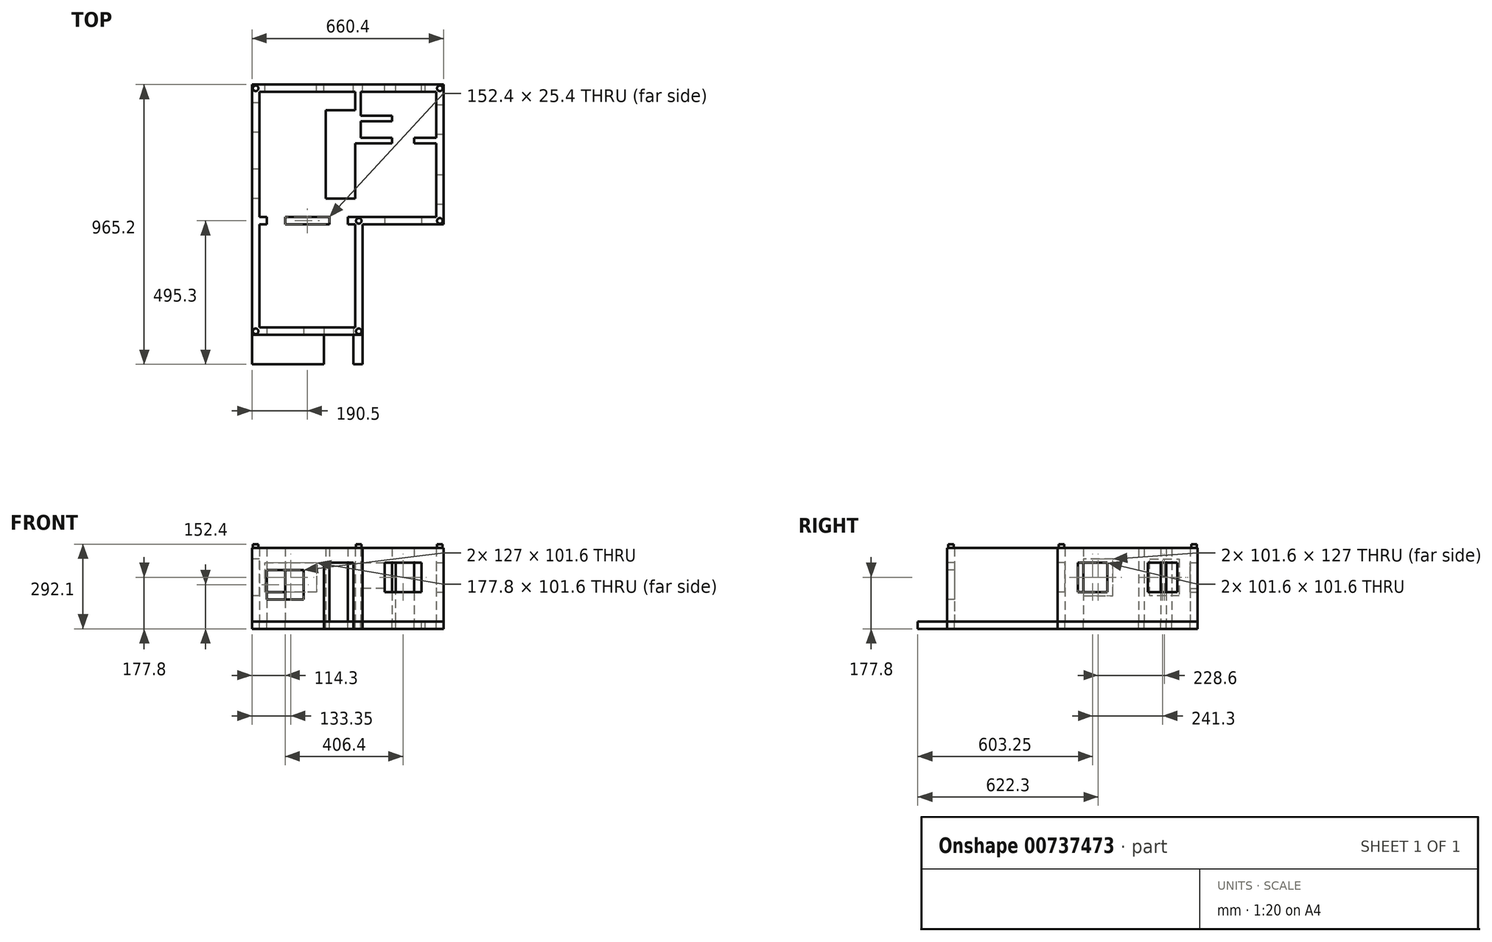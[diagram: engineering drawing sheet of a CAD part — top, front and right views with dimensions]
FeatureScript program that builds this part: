
annotation { "Feature Type Name" : "Feature", "Feature Type Description" : "" }
export const myFeature = defineFeature(function(context is Context, id is Id, definition is map)
    precondition{}
    {
        {
            var Q0;
            Q0=qCreatedBy(makeId("Top.planeOp"),FACE);
            var sketch = newSketch(context, id + "F0", { "sketchPlane" : qUnion([Q0])});
            skLineSegment(sketch, "E0", {"start": v(0, 0) * mm, "end": v(330.2, 0) * mm});
            skLineSegment(sketch, "E1", {"start": v(0, 0) * mm, "end": v(0, 381) * mm});
            skLineSegment(sketch, "E2", {"start": v(330.2, 0) * mm, "end": v(330.2, 381) * mm});
            skLineSegment(sketch, "E3", {"start": v(0, 381) * mm, "end": v(0, 812.8) * mm});
            skLineSegment(sketch, "E4", {"start": v(0, 812.8) * mm, "end": v(330.2, 812.8) * mm});
            skLineSegment(sketch, "E5", {"start": v(330.2, 381) * mm, "end": v(609.6, 381) * mm});
            skLineSegment(sketch, "E6", {"start": v(609.6, 381) * mm, "end": v(609.6, 812.8) * mm});
            skLineSegment(sketch, "E7", {"start": v(609.6, 635) * mm, "end": v(533.4, 635) * mm});
            skLineSegment(sketch, "E8", {"start": v(609.6, 812.8) * mm, "end": v(508, 812.8) * mm});
            skLineSegment(sketch, "E9", {"start": v(330.2, 812.8) * mm, "end": v(508, 812.8) * mm});
            skLineSegment(sketch, "E10", {"start": v(330.2, 672.42) * mm, "end": v(330.2, 812.8) * mm});
            skLineSegment(sketch, "E11", {"start": v(330.2, 635) * mm, "end": v(457.2, 635) * mm});
            skLineSegment(sketch, "E12", {"start": v(457.2, 711.2) * mm, "end": v(330.2, 711.2) * mm});
            skLineSegment(sketch, "E13", {"start": v(330.2, 0) * mm, "end": v(355.6, 0) * mm});
            skLineSegment(sketch, "E14", {"start": v(355.6, 0) * mm, "end": v(355.6, 355.6) * mm});
            skLineSegment(sketch, "E15", {"start": v(355.6, 355.6) * mm, "end": v(635, 355.6) * mm});
            skLineSegment(sketch, "E16", {"start": v(635, 355.6) * mm, "end": v(635, 838.2) * mm});
            skLineSegment(sketch, "E17", {"start": v(635, 838.2) * mm, "end": v(-25.4, 838.2) * mm});
            skLineSegment(sketch, "E18", {"start": v(-25.4, 838.2) * mm, "end": v(-25.4, -25.4) * mm});
            skLineSegment(sketch, "E19", {"start": v(-25.4, -25.4) * mm, "end": v(355.6, -25.4) * mm});
            skLineSegment(sketch, "E20", {"start": v(355.6, -25.4) * mm, "end": v(355.6, 0) * mm});
            skLineSegment(sketch, "E21", {"start": v(0, 381) * mm, "end": v(25.4, 381) * mm});
            skLineSegment(sketch, "E22", {"start": v(25.4, 381) * mm, "end": v(25.4, 355.6) * mm});
            skLineSegment(sketch, "E23", {"start": v(25.4, 355.6) * mm, "end": v(0, 355.6) * mm});
            skLineSegment(sketch, "E24", {"start": v(88.9, 381) * mm, "end": v(241.3, 381) * mm});
            skLineSegment(sketch, "E25", {"start": v(88.9, 381) * mm, "end": v(88.9, 355.6) * mm});
            skLineSegment(sketch, "E26", {"start": v(88.9, 355.6) * mm, "end": v(241.3, 355.6) * mm});
            skLineSegment(sketch, "E27", {"start": v(241.3, 355.6) * mm, "end": v(241.3, 381) * mm});
            skLineSegment(sketch, "E28", {"start": v(304.8, 355.6) * mm, "end": v(304.8, 381) * mm});
            skLineSegment(sketch, "E29", {"start": v(304.8, 381) * mm, "end": v(330.2, 381) * mm});
            skLineSegment(sketch, "E30", {"start": v(304.8, 355.6) * mm, "end": v(330.2, 355.6) * mm});
            skLineSegment(sketch, "E31", {"start": v(330.2, 672.42) * mm, "end": v(330.2, 635) * mm});
            skLineSegment(sketch, "E32", {"start": v(228.6, 749.3) * mm, "end": v(330.2, 749.3) * mm});
            skLineSegment(sketch, "E33", {"start": v(330.2, 635) * mm, "end": v(330.2, 444.5) * mm});
            skLineSegment(sketch, "E34", {"start": v(330.2, 444.5) * mm, "end": v(228.6, 444.5) * mm});
            skLineSegment(sketch, "E35", {"start": v(228.6, 444.5) * mm, "end": v(228.6, 749.3) * mm});
            skLineSegment(sketch, "E36", {"start": v(457.2, 711.2) * mm, "end": v(457.2, 730.25) * mm});
            skLineSegment(sketch, "E37", {"start": v(457.2, 635) * mm, "end": v(457.2, 654.05) * mm});
            skLineSegment(sketch, "E38", {"start": v(457.2, 654.05) * mm, "end": v(349.25, 654.05) * mm});
            skLineSegment(sketch, "E39", {"start": v(349.25, 654.05) * mm, "end": v(349.25, 711.2) * mm});
            skLineSegment(sketch, "E40", {"start": v(533.4, 635) * mm, "end": v(533.4, 654.05) * mm});
            skLineSegment(sketch, "E41", {"start": v(533.4, 654.05) * mm, "end": v(609.6, 654.05) * mm});
            skLineSegment(sketch, "E42", {"start": v(457.2, 730.25) * mm, "end": v(349.25, 730.25) * mm});
            skLineSegment(sketch, "E43", {"start": v(349.25, 730.25) * mm, "end": v(349.25, 812.8) * mm});
            skSolve(sketch);
        }
        {
            var Q0;
            {var subQ8=sQuery(id+"F0.wireOp",EDGE,"E0");Q0=makeQuery(id+"F0.imprint","IMPRINT",FACE,{"disambiguationData":[TD([[makeQuery(id+"F0.imprint","IMPRINT",EDGE,{"derivedFrom":subQ8}),-1.0]])]});}
            var Q1;
            Q1=makeQuery(id+"F0.imprint","IMPRINT",FACE,{"disambiguationData":[TD([[makeQuery(id+"F0.imprint","IMPRINT",EDGE,{"derivedFrom":sQuery(id+"F0.wireOp",EDGE,"E24")}),-1.0]])]});
            var Q2;
            {var subQ0=sQuery(id+"F0.wireOp",EDGE,"E21");Q2=makeQuery(id+"F0.imprint","IMPRINT",FACE,{"disambiguationData":[TD([[makeQuery(id+"F0.imprint","IMPRINT",EDGE,{"derivedFrom":subQ0}),-1.0]])]});}
            var Q3;
            Q3=makeQuery(id+"F0.imprint","IMPRINT",FACE,{"disambiguationData":[TD([[makeQuery(id+"F0.imprint","IMPRINT",EDGE,{"derivedFrom":sQuery(id+"F0.wireOp",EDGE,"E28")}),-1.0]])]});
            var Q4;
            {var subQ3=sQuery(id+"F0.wireOp",EDGE,"E31");Q4=makeQuery(id+"F0.imprint","IMPRINT",FACE,{"disambiguationData":[TD([[makeQuery(id+"F0.imprint","IMPRINT",EDGE,{"derivedFrom":subQ3}),-1.0]])]});}
            var Q5;
            {var subQ0=sQuery(id+"F0.wireOp",EDGE,"E36");Q5=makeQuery(id+"F0.imprint","IMPRINT",FACE,{"disambiguationData":[TD([[makeQuery(id+"F0.imprint","IMPRINT",EDGE,{"derivedFrom":subQ0}),1.0]])]});}
            var Q6;
            Q6=makeQuery(id+"F0.imprint","IMPRINT",FACE,{"disambiguationData":[TD([[makeQuery(id+"F0.imprint","IMPRINT",EDGE,{"derivedFrom":sQuery(id+"F0.wireOp",EDGE,"E11")}),1.0]])]});
            var Q7;
            {var subQ0=sQuery(id+"F0.wireOp",EDGE,"E7");Q7=makeQuery(id+"F0.imprint","IMPRINT",FACE,{"disambiguationData":[TD([[makeQuery(id+"F0.imprint","IMPRINT",EDGE,{"derivedFrom":subQ0}),-1.0]])]});}
            extrude(context, id + "F1", {"entities" : qUnion([Q0, Q1, Q2, Q3, Q4, Q5, Q6, Q7]), "depth" : 254 * mm, "offsetDistance" : 25.4 * mm});
        }
        {
            var Q0;
            {var subQ10=sQuery(id+"F0.wireOp",EDGE,"E0");Q0=makeQuery(id+"F0.imprint","IMPRINT",FACE,{"disambiguationData":[TD([[makeQuery(id+"F0.imprint","IMPRINT",EDGE,{"derivedFrom":subQ10}),1.0]])]});}
            extrude(context, id + "F2", {"entities" : qUnion([Q0]), "oppositeDirection" : true, "depth" : 25.4 * mm, "offsetDistance" : 25.4 * mm});
        }
        {
            var Q0;
            Q0=makeQuery(id+"F1.opExtrude","CAP_FACE",FACE,{"disambiguationData":[OSD([sQuery(id+"F0.wireOp",EDGE,"E0"),sQuery(id+"F0.wireOp",EDGE,"E1"),sQuery(id+"F0.wireOp",EDGE,"E2"),sQuery(id+"F0.wireOp",EDGE,"E3"),sQuery(id+"F0.wireOp",EDGE,"E4"),sQuery(id+"F0.wireOp",EDGE,"E5"),sQuery(id+"F0.wireOp",EDGE,"E6"),sQuery(id+"F0.wireOp",EDGE,"E7"),sQuery(id+"F0.wireOp",EDGE,"E8"),sQuery(id+"F0.wireOp",EDGE,"E9"),sQuery(id+"F0.wireOp",EDGE,"E10"),sQuery(id+"F0.wireOp",EDGE,"E11"),sQuery(id+"F0.wireOp",EDGE,"E12"),sQuery(id+"F0.wireOp",EDGE,"E14"),sQuery(id+"F0.wireOp",EDGE,"E15"),sQuery(id+"F0.wireOp",EDGE,"E16"),sQuery(id+"F0.wireOp",EDGE,"E17"),sQuery(id+"F0.wireOp",EDGE,"E18"),sQuery(id+"F0.wireOp",EDGE,"E19"),sQuery(id+"F0.wireOp",EDGE,"E20"),sQuery(id+"F0.wireOp",EDGE,"E21"),sQuery(id+"F0.wireOp",EDGE,"E22"),sQuery(id+"F0.wireOp",EDGE,"E23"),sQuery(id+"F0.wireOp",EDGE,"E28"),sQuery(id+"F0.wireOp",EDGE,"E29"),sQuery(id+"F0.wireOp",EDGE,"E30"),sQuery(id+"F0.wireOp",EDGE,"E32"),sQuery(id+"F0.wireOp",EDGE,"E33"),sQuery(id+"F0.wireOp",EDGE,"E34"),sQuery(id+"F0.wireOp",EDGE,"E35"),sQuery(id+"F0.wireOp",EDGE,"E36"),sQuery(id+"F0.wireOp",EDGE,"E37"),sQuery(id+"F0.wireOp",EDGE,"E38"),sQuery(id+"F0.wireOp",EDGE,"E39"),sQuery(id+"F0.wireOp",EDGE,"E40"),sQuery(id+"F0.wireOp",EDGE,"E41"),sQuery(id+"F0.wireOp",EDGE,"E42"),sQuery(id+"F0.wireOp",EDGE,"E43")])],"isStart":false});
            var sketch = newSketch(context, id + "F3", { "sketchPlane" : qUnion([Q0])});
            skLineSegment(sketch, "E44", {"start": v(0, 0) * mm, "end": v(-25.4, 0) * mm});
            skLineSegment(sketch, "E45", {"start": v(0, 0) * mm, "end": v(0, -25.4) * mm});
            skLineSegment(sketch, "E46", {"start": v(330.2, 0) * mm, "end": v(330.2, -25.4) * mm});
            skLineSegment(sketch, "E47", {"start": v(330.2, 0) * mm, "end": v(355.6, 0) * mm});
            skLineSegment(sketch, "E48", {"start": v(330.2, 355.6) * mm, "end": v(330.2, 381) * mm});
            skLineSegment(sketch, "E49", {"start": v(330.2, 355.6) * mm, "end": v(355.6, 355.6) * mm});
            skLineSegment(sketch, "E50", {"start": v(355.6, 355.6) * mm, "end": v(355.6, 381) * mm});
            skLineSegment(sketch, "E51", {"start": v(609.6, 381) * mm, "end": v(609.6, 355.6) * mm});
            skLineSegment(sketch, "E52", {"start": v(609.6, 381) * mm, "end": v(635, 381) * mm});
            skLineSegment(sketch, "E53", {"start": v(609.6, 812.8) * mm, "end": v(609.6, 838.2) * mm});
            skLineSegment(sketch, "E54", {"start": v(609.6, 812.8) * mm, "end": v(635, 812.8) * mm});
            skLineSegment(sketch, "E55", {"start": v(-25.4, 812.8) * mm, "end": v(0, 812.8) * mm});
            skLineSegment(sketch, "E56", {"start": v(0, 812.8) * mm, "end": v(0, 838.2) * mm});
            skCircle(sketch, "E57", {"center": v(-12.7, -12.7) * mm, "radius": 9.53 * mm});
            skPoint(sketch, "E57.centerSnap0", {"position": v(-12.7, 0) * mm});
            skPoint(sketch, "E57.centerSnap1", {"position": v(0, -12.7) * mm});
            skPoint(sketch, "E58.centerSnap0", {"position": v(330.2, -12.7) * mm});
            skPoint(sketch, "E58.centerSnap1", {"position": v(342.9, 0) * mm});
            skCircle(sketch, "E59", {"center": v(342.9, -12.7) * mm, "radius": 9.53 * mm});
            skCircle(sketch, "E60", {"center": v(342.9, 368.3) * mm, "radius": 9.53 * mm});
            skPoint(sketch, "E60.centerSnap0", {"position": v(342.9, 355.6) * mm});
            skPoint(sketch, "E60.centerSnap1", {"position": v(330.2, 368.3) * mm});
            skCircle(sketch, "E61", {"center": v(622.3, 368.3) * mm, "radius": 9.53 * mm});
            skPoint(sketch, "E61.centerSnap0", {"position": v(609.6, 368.3) * mm});
            skPoint(sketch, "E61.centerSnap1", {"position": v(622.3, 381) * mm});
            skCircle(sketch, "E62", {"center": v(622.3, 825.5) * mm, "radius": 9.53 * mm});
            skPoint(sketch, "E62.centerSnap0", {"position": v(609.6, 825.5) * mm});
            skPoint(sketch, "E62.centerSnap1", {"position": v(622.3, 812.8) * mm});
            skCircle(sketch, "E63", {"center": v(-12.7, 825.5) * mm, "radius": 9.53 * mm});
            skPoint(sketch, "E63.centerSnap0", {"position": v(-12.7, 812.8) * mm});
            skPoint(sketch, "E63.centerSnap1", {"position": v(0, 825.5) * mm});
            skSolve(sketch);
        }
        {
            var Q0;
            Q0=qSketchRegion(id+"F3",true);
            extrude(context, id + "F4", {"entities" : qUnion([Q0]), "operationType" : NewBodyOperationType.ADD, "depth" : 12.7 * mm, "offsetDistance" : 25.4 * mm});
        }
        {
            var Q0;
            Q0=makeQuery(id+"F1.opExtrude","SWEPT_FACE",FACE,{"disambiguationData":[OSD([sQuery(id+"F0.wireOp",EDGE,"E19")])]});
            var sketch = newSketch(context, id + "F5", { "sketchPlane" : qUnion([Q0])});
            skLineSegment(sketch, "E64", {"start": v(-25.4, 0) * mm, "end": v(-25.4, 76.2) * mm});
            skLineSegment(sketch, "E65", {"start": v(25.4, 76.2) * mm, "end": v(152.4, 76.2) * mm});
            skLineSegment(sketch, "E66", {"start": v(152.4, 76.2) * mm, "end": v(152.4, 177.8) * mm});
            skLineSegment(sketch, "E67", {"start": v(152.4, 177.8) * mm, "end": v(25.4, 177.8) * mm});
            skLineSegment(sketch, "E68", {"start": v(25.4, 177.8) * mm, "end": v(25.4, 76.2) * mm});
            skSolve(sketch);
        }
        {
            var Q0;
            Q0=makeQuery(id+"F5.imprint","IMPRINT",FACE,{"disambiguationData":[TD([[makeQuery(id+"F5.imprint","IMPRINT",EDGE,{"derivedFrom":sQuery(id+"F5.wireOp",EDGE,"E65")}),1.0]])]});
            extrude(context, id + "F6", {"entities" : qUnion([Q0]), "operationType" : NewBodyOperationType.REMOVE, "oppositeDirection" : true, "depth" : 25.4 * mm, "offsetDistance" : 25.4 * mm});
        }
        {
            var Q0;
            Q0=makeQuery(id+"F1.opExtrude","SWEPT_FACE",FACE,{"disambiguationData":[OSD([sQuery(id+"F0.wireOp",EDGE,"E19")])]});
            var sketch = newSketch(context, id + "F7", { "sketchPlane" : qUnion([Q0])});
            skLineSegment(sketch, "E69", {"start": v(323.85, 0) * mm, "end": v(323.85, 203.2) * mm});
            skLineSegment(sketch, "E70", {"start": v(323.85, 203.2) * mm, "end": v(222.25, 203.2) * mm});
            skLineSegment(sketch, "E71", {"start": v(222.25, 203.2) * mm, "end": v(222.25, 0) * mm});
            skLineSegment(sketch, "E72", {"start": v(222.25, 0) * mm, "end": v(323.85, 0) * mm});
            skSolve(sketch);
        }
        {
            var Q0;
            Q0=qSketchRegion(id+"F7",true);
            extrude(context, id + "F8", {"entities" : qUnion([Q0]), "operationType" : NewBodyOperationType.REMOVE, "oppositeDirection" : true, "depth" : 25.4 * mm, "offsetDistance" : 25.4 * mm});
        }
        {
            var Q0;
            Q0=makeQuery(id+"F1.opExtrude","SWEPT_FACE",FACE,{"disambiguationData":[OSD([sQuery(id+"F0.wireOp",EDGE,"E15")])]});
            var sketch = newSketch(context, id + "F9", { "sketchPlane" : qUnion([Q0])});
            skLineSegment(sketch, "E73", {"start": v(395.93, 254) * mm, "end": v(395.93, 0) * mm});
            skLineSegment(sketch, "E74", {"start": v(355.6, 231.93) * mm, "end": v(635, 231.93) * mm});
            skPoint(sketch, "E75.startSnap0", {"position": v(395.93, 127) * mm});
            skPoint(sketch, "E75.startSnap1", {"position": v(495.3, 231.93) * mm});
            skLineSegment(sketch, "E76", {"start": v(495.3, 101.6) * mm, "end": v(431.8, 101.6) * mm});
            skLineSegment(sketch, "E77", {"start": v(431.8, 101.6) * mm, "end": v(431.8, 203.2) * mm});
            skLineSegment(sketch, "E78", {"start": v(431.8, 203.2) * mm, "end": v(558.8, 203.2) * mm});
            skLineSegment(sketch, "E79", {"start": v(558.8, 203.2) * mm, "end": v(558.8, 101.6) * mm});
            skLineSegment(sketch, "E80", {"start": v(558.8, 101.6) * mm, "end": v(495.3, 101.6) * mm});
            skSolve(sketch);
        }
        {
            var Q0;
            Q0=qSketchRegion(id+"F9",true);
            extrude(context, id + "F10", {"entities" : qUnion([Q0]), "operationType" : NewBodyOperationType.REMOVE, "oppositeDirection" : true, "depth" : 25.4 * mm, "offsetDistance" : 25.4 * mm});
        }
        {
            var Q0;
            Q0=makeQuery(id+"F1.opExtrude","SWEPT_FACE",FACE,{"disambiguationData":[OSD([sQuery(id+"F0.wireOp",EDGE,"E16")])]});
            var sketch = newSketch(context, id + "F11", { "sketchPlane" : qUnion([Q0])});
            skLineSegment(sketch, "E81", {"start": v(355.6, 254) * mm, "end": v(838.2, 254) * mm});
            skLineSegment(sketch, "E82", {"start": v(596.9, 254) * mm, "end": v(596.9, 0) * mm});
            skLineSegment(sketch, "E83", {"start": v(355.6, 254) * mm, "end": v(596.9, 254) * mm});
            skLineSegment(sketch, "E84", {"start": v(476.25, 203.2) * mm, "end": v(425.45, 203.2) * mm});
            skLineSegment(sketch, "E85", {"start": v(425.45, 203.2) * mm, "end": v(425.45, 101.6) * mm});
            skLineSegment(sketch, "E86", {"start": v(425.45, 101.6) * mm, "end": v(527.05, 101.6) * mm});
            skLineSegment(sketch, "E87", {"start": v(527.05, 101.6) * mm, "end": v(527.05, 203.2) * mm});
            skLineSegment(sketch, "E88", {"start": v(527.05, 203.2) * mm, "end": v(476.25, 203.2) * mm});
            skLineSegment(sketch, "E89", {"start": v(596.9, 254) * mm, "end": v(838.2, 254) * mm});
            skLineSegment(sketch, "E90", {"start": v(717.55, 203.2) * mm, "end": v(666.75, 203.2) * mm});
            skLineSegment(sketch, "E91", {"start": v(666.75, 203.2) * mm, "end": v(666.75, 101.6) * mm});
            skLineSegment(sketch, "E92", {"start": v(666.75, 101.6) * mm, "end": v(768.35, 101.6) * mm});
            skLineSegment(sketch, "E93", {"start": v(768.35, 101.6) * mm, "end": v(768.35, 203.2) * mm});
            skLineSegment(sketch, "E94", {"start": v(768.35, 203.2) * mm, "end": v(717.55, 203.2) * mm});
            skSolve(sketch);
        }
        {
            var Q0;
            Q0=qSketchRegion(id+"F11",true);
            extrude(context, id + "F12", {"entities" : qUnion([Q0]), "operationType" : NewBodyOperationType.REMOVE, "oppositeDirection" : true, "depth" : 25.4 * mm, "offsetDistance" : 25.4 * mm});
        }
        {
            var Q0;
            Q0=qSketchRegion(id+"F11",true);
            extrude(context, id + "F13", {"entities" : qUnion([Q0]), "operationType" : NewBodyOperationType.REMOVE, "oppositeDirection" : true, "depth" : 25.4 * mm, "offsetDistance" : 25.4 * mm});
        }
        {
            var Q0;
            Q0=makeQuery(id+"F1.opExtrude","SWEPT_FACE",FACE,{"disambiguationData":[OSD([sQuery(id+"F0.wireOp",EDGE,"E18")])]});
            var sketch = newSketch(context, id + "F14", { "sketchPlane" : qUnion([Q0])});
            skLineSegment(sketch, "E95", {"start": v(-838.2, 254) * mm, "end": v(-381, 254) * mm});
            skLineSegment(sketch, "E96", {"start": v(-381, 254) * mm, "end": v(-381, 0) * mm});
            skLineSegment(sketch, "E97", {"start": v(-609.6, 254) * mm, "end": v(-609.6, 0) * mm});
            skLineSegment(sketch, "E98", {"start": v(-838.2, 254) * mm, "end": v(-609.6, 254) * mm});
            skLineSegment(sketch, "E99", {"start": v(-723.9, 215.9) * mm, "end": v(-774.7, 215.9) * mm});
            skLineSegment(sketch, "E100", {"start": v(-774.7, 215.9) * mm, "end": v(-774.7, 88.9) * mm});
            skLineSegment(sketch, "E101", {"start": v(-774.7, 88.9) * mm, "end": v(-673.1, 88.9) * mm});
            skLineSegment(sketch, "E102", {"start": v(-673.1, 88.9) * mm, "end": v(-673.1, 215.9) * mm});
            skLineSegment(sketch, "E103", {"start": v(-673.1, 215.9) * mm, "end": v(-723.9, 215.9) * mm});
            skLineSegment(sketch, "E104.MirrorCS", {"start": v(-546.1, 88.9) * mm, "end": v(-546.1, 215.9) * mm});
            skLineSegment(sketch, "E105.MirrorCS", {"start": v(-546.1, 215.9) * mm, "end": v(-495.3, 215.9) * mm});
            skLineSegment(sketch, "E106.MirrorCS", {"start": v(-495.3, 215.9) * mm, "end": v(-444.5, 215.9) * mm});
            skLineSegment(sketch, "E107.MirrorCS", {"start": v(-444.5, 215.9) * mm, "end": v(-444.5, 88.9) * mm});
            skLineSegment(sketch, "E108.MirrorCS", {"start": v(-444.5, 88.9) * mm, "end": v(-546.1, 88.9) * mm});
            skSolve(sketch);
        }
        {
            var Q0;
            Q0=qSketchRegion(id+"F14",true);
            extrude(context, id + "F15", {"entities" : qUnion([Q0]), "operationType" : NewBodyOperationType.REMOVE, "oppositeDirection" : true, "depth" : 25.4 * mm, "offsetDistance" : 25.4 * mm});
        }
        {
            var Q0;
            Q0=qSketchRegion(id+"F14",true);
            extrude(context, id + "F16", {"entities" : qUnion([Q0]), "operationType" : NewBodyOperationType.REMOVE, "oppositeDirection" : true, "depth" : 25.4 * mm, "offsetDistance" : 25.4 * mm});
        }
        {
            var Q0;
            Q0=makeQuery(id+"F1.opExtrude","SWEPT_FACE",FACE,{"disambiguationData":[OSD([sQuery(id+"F0.wireOp",EDGE,"E17")])]});
            var sketch = newSketch(context, id + "F17", { "sketchPlane" : qUnion([Q0])});
            skLineSegment(sketch, "E109", {"start": v(25.4, 254) * mm, "end": v(-330.2, 254) * mm});
            skLineSegment(sketch, "E110", {"start": v(-330.2, 254) * mm, "end": v(-330.2, 0) * mm});
            skPoint(sketch, "E111.endSnap0", {"position": v(-152.4, 254) * mm});
            skLineSegment(sketch, "E112", {"start": v(-222.25, 0) * mm, "end": v(-222.25, 203.2) * mm});
            skLineSegment(sketch, "E113", {"start": v(-222.25, 203.2) * mm, "end": v(-323.85, 203.2) * mm});
            skLineSegment(sketch, "E114", {"start": v(-323.85, 203.2) * mm, "end": v(-323.85, 0) * mm});
            skLineSegment(sketch, "E115", {"start": v(-323.85, 0) * mm, "end": v(-222.25, 0) * mm});
            skLineSegment(sketch, "E116", {"start": v(-196.85, 203.2) * mm, "end": v(-196.85, 101.6) * mm});
            skLineSegment(sketch, "E117", {"start": v(-196.85, 101.6) * mm, "end": v(-19.05, 101.6) * mm});
            skLineSegment(sketch, "E118", {"start": v(-19.05, 101.6) * mm, "end": v(-19.05, 203.2) * mm});
            skLineSegment(sketch, "E119", {"start": v(-19.05, 203.2) * mm, "end": v(-196.85, 203.2) * mm});
            skSolve(sketch);
        }
        {
            var Q0;
            Q0=qSketchRegion(id+"F17",true);
            extrude(context, id + "F18", {"entities" : qUnion([Q0]), "operationType" : NewBodyOperationType.REMOVE, "oppositeDirection" : true, "depth" : 25.4 * mm, "offsetDistance" : 25.4 * mm});
        }
        {
            var Q0;
            Q0=qSketchRegion(id+"F17",true);
            extrude(context, id + "F19", {"entities" : qUnion([Q0]), "operationType" : NewBodyOperationType.REMOVE, "oppositeDirection" : true, "depth" : 25.4 * mm, "offsetDistance" : 25.4 * mm});
        }
        {
            var Q0;
            Q0=makeQuery(id+"F1.opExtrude","SWEPT_FACE",FACE,{"disambiguationData":[OSD([sQuery(id+"F0.wireOp",EDGE,"E17")])]});
            var sketch = newSketch(context, id + "F20", { "sketchPlane" : qUnion([Q0])});
            skLineSegment(sketch, "E120", {"start": v(-635, 254) * mm, "end": v(-355.6, 254) * mm});
            skLineSegment(sketch, "E121", {"start": v(-355.6, 139.7) * mm, "end": v(-355.6, 203.2) * mm});
            skLineSegment(sketch, "E122", {"start": v(-355.6, 203.2) * mm, "end": v(-431.8, 203.2) * mm});
            skLineSegment(sketch, "E123", {"start": v(-431.8, 203.2) * mm, "end": v(-431.8, 114.3) * mm});
            skLineSegment(sketch, "E124", {"start": v(-431.8, 114.3) * mm, "end": v(-355.6, 114.3) * mm});
            skLineSegment(sketch, "E125", {"start": v(-355.6, 114.3) * mm, "end": v(-355.6, 139.7) * mm});
            skLineSegment(sketch, "E126", {"start": v(-431.8, 114.3) * mm, "end": v(-469.9, 114.3) * mm});
            skLineSegment(sketch, "E127", {"start": v(-469.9, 114.3) * mm, "end": v(-469.9, 203.2) * mm});
            skLineSegment(sketch, "E128", {"start": v(-469.9, 203.2) * mm, "end": v(-558.8, 203.2) * mm});
            skLineSegment(sketch, "E129", {"start": v(-558.8, 203.2) * mm, "end": v(-558.8, 0) * mm});
            skLineSegment(sketch, "E130", {"start": v(-558.8, 0) * mm, "end": v(-469.9, 0) * mm});
            skLineSegment(sketch, "E131", {"start": v(-469.9, 0) * mm, "end": v(-469.9, 114.3) * mm});
            skSolve(sketch);
        }
        {
            var Q0;
            Q0=makeQuery(id+"F20.imprint","IMPRINT",FACE,{"disambiguationData":[TD([[makeQuery(id+"F20.imprint","IMPRINT",EDGE,{"derivedFrom":sQuery(id+"F20.wireOp",EDGE,"E121")}),1.0]])]});
            extrude(context, id + "F21", {"entities" : qUnion([Q0]), "operationType" : NewBodyOperationType.REMOVE, "oppositeDirection" : true, "depth" : 25.4 * mm, "offsetDistance" : 25.4 * mm});
        }
        {
            var Q0;
            Q0=qSketchRegion(id+"F20",true);
            extrude(context, id + "F22", {"entities" : qUnion([Q0]), "operationType" : NewBodyOperationType.REMOVE, "oppositeDirection" : true, "depth" : 25.4 * mm, "offsetDistance" : 25.4 * mm});
        }
        {
            var Q0;
            {var subQ0=sQuery(id+"F0.wireOp",EDGE,"E32");var subQ2=sQuery(id+"F0.wireOp",EDGE,"E17");var subQ4=sQuery(id+"F0.wireOp",EDGE,"E12");var subQ6=sQuery(id+"F0.wireOp",EDGE,"E37");var subQ8=sQuery(id+"F0.wireOp",EDGE,"E4");var subQ9=makeQuery(id+"F1.opExtrude","SWEPT_FACE",FACE,{"disambiguationData":[OSD([subQ8])]});var subQ10=sQuery(id+"F0.wireOp",EDGE,"E33");var subQ12=sQuery(id+"F0.wireOp",EDGE,"E9");var subQ13=sQuery(id+"F0.wireOp",EDGE,"E8");var subQ15=sQuery(id+"F0.wireOp",EDGE,"E34");var subQ17=sQuery(id+"F0.wireOp",EDGE,"E10");var subQ19=sQuery(id+"F0.wireOp",EDGE,"E35");var subQ21=sQuery(id+"F0.wireOp",EDGE,"E11");var subQ23=sQuery(id+"F0.wireOp",EDGE,"E36");var subQ26=sQuery(id+"F0.wireOp",EDGE,"E38");var subQ28=sQuery(id+"F0.wireOp",EDGE,"E39");var subQ30=sQuery(id+"F0.wireOp",EDGE,"E42");var subQ32=sQuery(id+"F0.wireOp",EDGE,"E43");var subQ34=sQuery(id+"F0.wireOp",EDGE,"E19");var subQ35=sQuery(id+"F0.wireOp",EDGE,"E16");var subQ36=sQuery(id+"F0.wireOp",EDGE,"E15");var subQ37=sQuery(id+"F0.wireOp",EDGE,"E20");var subQ38=sQuery(id+"F0.wireOp",EDGE,"E14");var subQ39=sQuery(id+"F0.wireOp",EDGE,"E28");var subQ40=sQuery(id+"F0.wireOp",EDGE,"E29");var subQ41=sQuery(id+"F0.wireOp",EDGE,"E5");var subQ42=sQuery(id+"F0.wireOp",EDGE,"E2");var subQ43=sQuery(id+"F0.wireOp",EDGE,"E0");var subQ44=sQuery(id+"F0.wireOp",EDGE,"E30");var subQ45=sQuery(id+"F0.wireOp",EDGE,"E6");var subQ46=sQuery(id+"F0.wireOp",EDGE,"E7");var subQ47=sQuery(id+"F0.wireOp",EDGE,"E41");var subQ48=sQuery(id+"F0.wireOp",EDGE,"E40");Q0=makeQuery(id+"F22.boolean.opBoolean","SPLIT",FACE,{"disambiguationData":[TD([subQ9])],"derivedFrom":makeQuery(id+"F18.boolean.opBoolean","SPLIT",FACE,{"disambiguationData":[TD([makeQuery(id+"F1.opExtrude","SWEPT_FACE",FACE,{"disambiguationData":[OSD([subQ42])]})])],"derivedFrom":makeQuery(id+"F1.opExtrude","CAP_FACE",FACE,{"disambiguationData":[OSD([subQ43,sQuery(id+"F0.wireOp",EDGE,"E1"),subQ42,sQuery(id+"F0.wireOp",EDGE,"E3"),subQ8,subQ41,subQ45,subQ46,subQ13,subQ12,subQ17,subQ21,subQ4,subQ38,subQ36,subQ35,subQ2,sQuery(id+"F0.wireOp",EDGE,"E18"),subQ34,subQ37,sQuery(id+"F0.wireOp",EDGE,"E21"),sQuery(id+"F0.wireOp",EDGE,"E22"),sQuery(id+"F0.wireOp",EDGE,"E23"),subQ39,subQ40,subQ44,subQ0,subQ10,subQ15,subQ19,subQ23,subQ6,subQ26,subQ28,subQ48,subQ47,subQ30,subQ32])],"isStart":true})})});}
            var Q1;
            {var subQ0=sQuery(id+"F0.wireOp",EDGE,"E16");var subQ2=sQuery(id+"F0.wireOp",EDGE,"E40");var subQ4=sQuery(id+"F0.wireOp",EDGE,"E15");var subQ6=sQuery(id+"F0.wireOp",EDGE,"E7");var subQ8=sQuery(id+"F0.wireOp",EDGE,"E8");var subQ9=sQuery(id+"F0.wireOp",EDGE,"E6");var subQ10=sQuery(id+"F0.wireOp",EDGE,"E41");var subQ12=sQuery(id+"F0.wireOp",EDGE,"E9");var subQ14=sQuery(id+"F0.wireOp",EDGE,"E0");var subQ15=makeQuery(id+"F1.opExtrude","SWEPT_FACE",FACE,{"disambiguationData":[OSD([subQ14])]});var subQ16=sQuery(id+"F0.wireOp",EDGE,"E20");var subQ17=sQuery(id+"F0.wireOp",EDGE,"E14");var subQ19=sQuery(id+"F0.wireOp",EDGE,"E2");var subQ20=makeQuery(id+"F1.opExtrude","SWEPT_FACE",FACE,{"disambiguationData":[OSD([subQ19])]});var subQ21=sQuery(id+"F0.wireOp",EDGE,"E29");var subQ22=sQuery(id+"F0.wireOp",EDGE,"E5");var subQ24=sQuery(id+"F0.wireOp",EDGE,"E28");var subQ27=sQuery(id+"F0.wireOp",EDGE,"E30");var subQ29=sQuery(id+"F0.wireOp",EDGE,"E17");var subQ32=sQuery(id+"F0.wireOp",EDGE,"E19");var subQ35=sQuery(id+"F0.wireOp",EDGE,"E12");var subQ36=sQuery(id+"F0.wireOp",EDGE,"E4");var subQ37=sQuery(id+"F0.wireOp",EDGE,"E34");var subQ38=sQuery(id+"F0.wireOp",EDGE,"E32");var subQ39=sQuery(id+"F0.wireOp",EDGE,"E33");var subQ40=sQuery(id+"F0.wireOp",EDGE,"E35");var subQ41=sQuery(id+"F0.wireOp",EDGE,"E10");var subQ42=sQuery(id+"F0.wireOp",EDGE,"E11");var subQ43=sQuery(id+"F0.wireOp",EDGE,"E36");var subQ44=sQuery(id+"F0.wireOp",EDGE,"E37");var subQ45=sQuery(id+"F0.wireOp",EDGE,"E38");var subQ46=sQuery(id+"F0.wireOp",EDGE,"E39");var subQ47=sQuery(id+"F0.wireOp",EDGE,"E42");var subQ48=sQuery(id+"F0.wireOp",EDGE,"E43");Q1=makeQuery(id+"F22.boolean.opBoolean","SPLIT",FACE,{"disambiguationData":[TD([subQ15])],"derivedFrom":makeQuery(id+"F18.boolean.opBoolean","SPLIT",FACE,{"disambiguationData":[TD([subQ20])],"derivedFrom":makeQuery(id+"F1.opExtrude","CAP_FACE",FACE,{"disambiguationData":[OSD([subQ14,sQuery(id+"F0.wireOp",EDGE,"E1"),subQ19,sQuery(id+"F0.wireOp",EDGE,"E3"),subQ36,subQ22,subQ9,subQ6,subQ8,subQ12,subQ41,subQ42,subQ35,subQ17,subQ4,subQ0,subQ29,sQuery(id+"F0.wireOp",EDGE,"E18"),subQ32,subQ16,sQuery(id+"F0.wireOp",EDGE,"E21"),sQuery(id+"F0.wireOp",EDGE,"E22"),sQuery(id+"F0.wireOp",EDGE,"E23"),subQ24,subQ21,subQ27,subQ38,subQ39,subQ37,subQ40,subQ43,subQ44,subQ45,subQ46,subQ2,subQ10,subQ47,subQ48])],"isStart":true})})});}
            var Q2;
            {var subQ0=sQuery(id+"F0.wireOp",EDGE,"E23");var subQ1=sQuery(id+"F0.wireOp",EDGE,"E0");var subQ2=sQuery(id+"F0.wireOp",EDGE,"E21");var subQ3=sQuery(id+"F0.wireOp",EDGE,"E19");var subQ4=sQuery(id+"F0.wireOp",EDGE,"E18");var subQ5=sQuery(id+"F0.wireOp",EDGE,"E17");var subQ6=sQuery(id+"F0.wireOp",EDGE,"E22");var subQ7=sQuery(id+"F0.wireOp",EDGE,"E3");var subQ8=sQuery(id+"F0.wireOp",EDGE,"E1");var subQ9=sQuery(id+"F0.wireOp",EDGE,"E4");Q2=makeQuery(id+"F18.boolean.opBoolean","SPLIT",FACE,{"disambiguationData":[TD([makeQuery(id+"F1.opExtrude","SWEPT_FACE",FACE,{"disambiguationData":[OSD([subQ8])]})])],"derivedFrom":makeQuery(id+"F1.opExtrude","CAP_FACE",FACE,{"disambiguationData":[OSD([subQ1,subQ8,sQuery(id+"F0.wireOp",EDGE,"E2"),subQ7,subQ9,sQuery(id+"F0.wireOp",EDGE,"E5"),sQuery(id+"F0.wireOp",EDGE,"E6"),sQuery(id+"F0.wireOp",EDGE,"E7"),sQuery(id+"F0.wireOp",EDGE,"E8"),sQuery(id+"F0.wireOp",EDGE,"E9"),sQuery(id+"F0.wireOp",EDGE,"E10"),sQuery(id+"F0.wireOp",EDGE,"E11"),sQuery(id+"F0.wireOp",EDGE,"E12"),sQuery(id+"F0.wireOp",EDGE,"E14"),sQuery(id+"F0.wireOp",EDGE,"E15"),sQuery(id+"F0.wireOp",EDGE,"E16"),subQ5,subQ4,subQ3,sQuery(id+"F0.wireOp",EDGE,"E20"),subQ2,subQ6,subQ0,sQuery(id+"F0.wireOp",EDGE,"E28"),sQuery(id+"F0.wireOp",EDGE,"E29"),sQuery(id+"F0.wireOp",EDGE,"E30"),sQuery(id+"F0.wireOp",EDGE,"E32"),sQuery(id+"F0.wireOp",EDGE,"E33"),sQuery(id+"F0.wireOp",EDGE,"E34"),sQuery(id+"F0.wireOp",EDGE,"E35"),sQuery(id+"F0.wireOp",EDGE,"E36"),sQuery(id+"F0.wireOp",EDGE,"E37"),sQuery(id+"F0.wireOp",EDGE,"E38"),sQuery(id+"F0.wireOp",EDGE,"E39"),sQuery(id+"F0.wireOp",EDGE,"E40"),sQuery(id+"F0.wireOp",EDGE,"E41"),sQuery(id+"F0.wireOp",EDGE,"E42"),sQuery(id+"F0.wireOp",EDGE,"E43")])],"isStart":true})});}
            extrude(context, id + "F23", {"entities" : qUnion([Q0, Q1, Q2]), "depth" : 25.4 * mm, "offsetDistance" : 25.4 * mm});
        }
        {
            var Q0;
            Q0=makeQuery(id+"F23.opExtrude","SWEPT_FACE",FACE,{"disambiguationData":[OSD([sQuery(id+"F0.wireOp",EDGE,"E19"),sQuery(id+"F7.wireOp",EDGE,"E71"),sQuery(id+"F7.wireOp",EDGE,"E72")])]});
            extrude(context, id + "F24", {"entities" : qUnion([Q0]), "depth" : 101.6 * mm, "offsetDistance" : 25.4 * mm});
        }
        {
            var Q0;
            Q0=makeQuery(id+"F23.opExtrude","SWEPT_FACE",FACE,{"disambiguationData":[OSD([sQuery(id+"F0.wireOp",EDGE,"E17"),sQuery(id+"F17.wireOp",EDGE,"E112"),sQuery(id+"F17.wireOp",EDGE,"E115")])]});
            var Q1;
            Q1=makeQuery(id+"F23.opExtrude","SWEPT_FACE",FACE,{"disambiguationData":[OSD([sQuery(id+"F0.wireOp",EDGE,"E17"),sQuery(id+"F20.wireOp",EDGE,"E130"),sQuery(id+"F20.wireOp",EDGE,"E131")])]});
            extrude(context, id + "F25", {"entities" : qUnion([Q0, Q1]), "depth" : 101.6 * mm, "offsetDistance" : 25.4 * mm});
        }
    });
